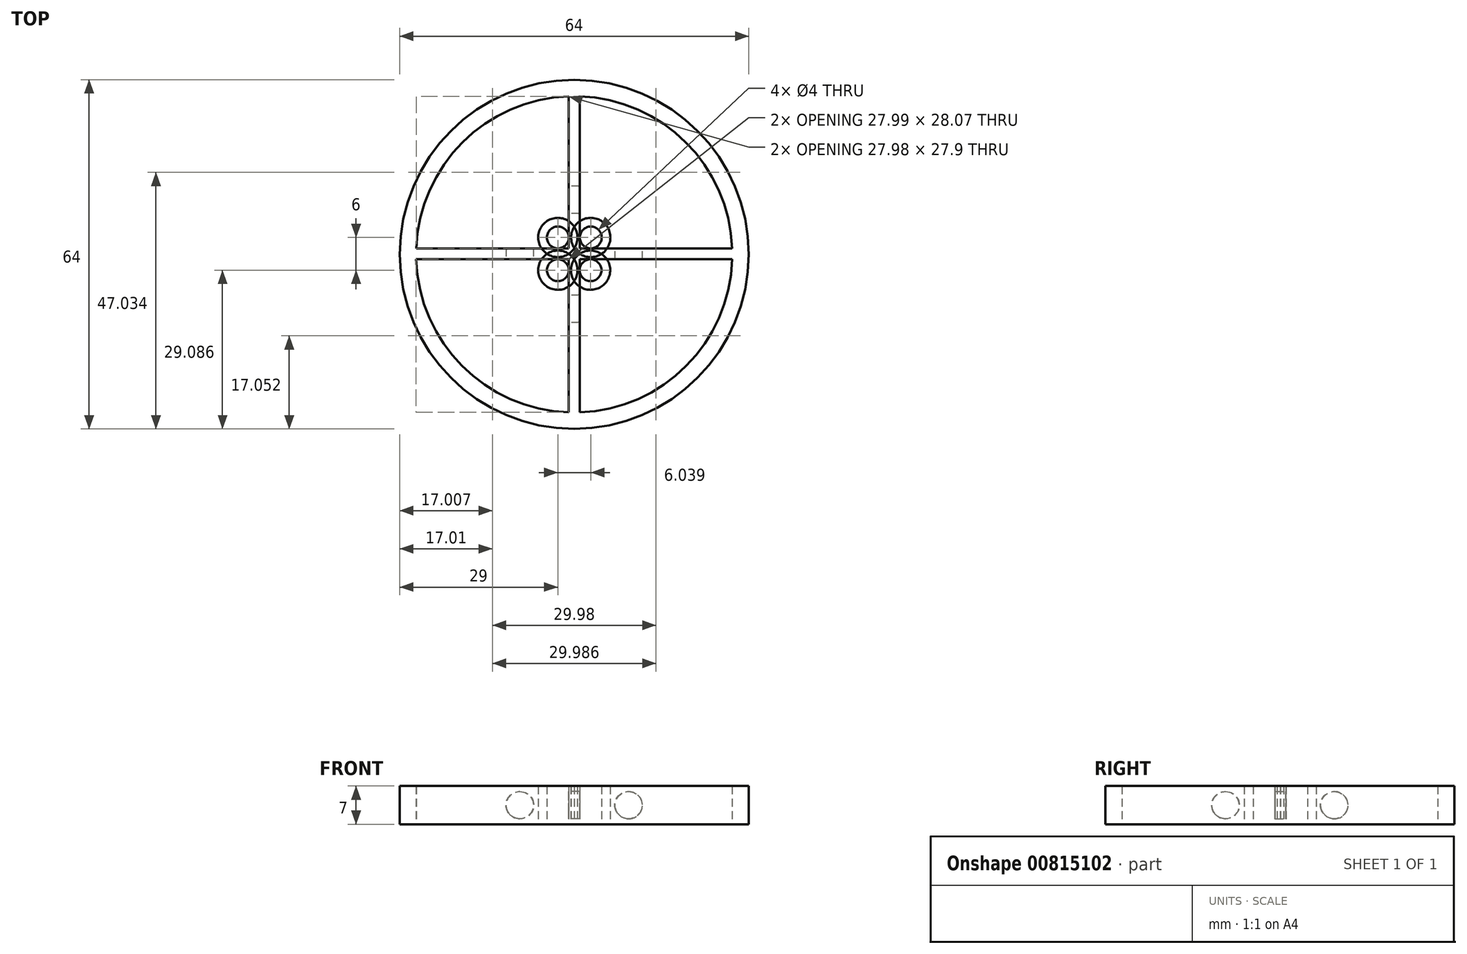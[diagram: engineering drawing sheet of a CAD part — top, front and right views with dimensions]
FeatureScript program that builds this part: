
annotation { "Feature Type Name" : "Feature", "Feature Type Description" : "" }
export const myFeature = defineFeature(function(context is Context, id is Id, definition is map)
    precondition{}
    {
        {
            var Q0;
            Q0=qCreatedBy(makeId("Top.planeOp"),FACE);
            var sketch = newSketch(context, id + "F0", { "sketchPlane" : qUnion([Q0])});
            skCircle(sketch, "E0", {"center": v(0, 0) * mm, "radius": 32 * mm});
            skCircle(sketch, "E1", {"center": v(0, 0) * mm, "radius": 29 * mm});
            skLineSegment(sketch, "E2.bottom", {"start": v(-1, 29.98) * mm, "end": v(1, 29.98) * mm});
            skLineSegment(sketch, "E2.top", {"start": v(-1, -29.98) * mm, "end": v(1, -29.98) * mm});
            skLineSegment(sketch, "E2.left", {"start": v(-1, 29.98) * mm, "end": v(-1, -29.98) * mm});
            skLineSegment(sketch, "E2.right", {"start": v(1, 29.98) * mm, "end": v(1, -29.98) * mm});
            skLineSegment(sketch, "E3.bottom", {"start": v(29.99, 1.09) * mm, "end": v(29.99, -0.91) * mm});
            skLineSegment(sketch, "E3.top", {"start": v(-29.98, 1.09) * mm, "end": v(-29.98, -0.91) * mm});
            skLineSegment(sketch, "E3.left", {"start": v(29.99, 1.09) * mm, "end": v(-29.98, 1.09) * mm});
            skLineSegment(sketch, "E3.right", {"start": v(29.99, -0.91) * mm, "end": v(-29.98, -0.91) * mm});
            skSolve(sketch);
        }
        {
            var Q0;
            Q0=makeQuery(id+"F0.imprint","IMPRINT",FACE,{"disambiguationData":[TD([[makeQuery(id+"F0.imprint","IMPRINT",EDGE,{"derivedFrom":sQuery(id+"F0.wireOp",EDGE,"E0")}),1.0]])]});
            var Q1;
            {var subQ0=sQuery(id+"F0.wireOp",EDGE,"E2.bottom");Q1=makeQuery(id+"F0.imprint","IMPRINT",FACE,{"disambiguationData":[TD([[makeQuery(id+"F0.imprint","IMPRINT",EDGE,{"derivedFrom":subQ0}),-1.0]])]});}
            var Q2;
            {var subQ5=sQuery(id+"F0.wireOp",EDGE,"E3.top");Q2=makeQuery(id+"F0.imprint","IMPRINT",FACE,{"disambiguationData":[TD([[makeQuery(id+"F0.imprint","IMPRINT",EDGE,{"derivedFrom":subQ5}),1.0]])]});}
            var Q3;
            {var subQ0=sQuery(id+"F0.wireOp",EDGE,"E2.top");Q3=makeQuery(id+"F0.imprint","IMPRINT",FACE,{"disambiguationData":[TD([[makeQuery(id+"F0.imprint","IMPRINT",EDGE,{"derivedFrom":subQ0}),1.0]])]});}
            var Q4;
            {var subQ0=sQuery(id+"F0.wireOp",EDGE,"E3.left");var subQ1=sQuery(id+"F0.wireOp",EDGE,"E2.left");var subQ2=makeQuery(id+"F0.imprint","INTERSECT",VERTEX,{"derivedFrom":[subQ1,subQ0]});Q4=makeQuery(id+"F0.imprint","IMPRINT",FACE,{"disambiguationData":[TD([[makeQuery(id+"F0.imprint","IMPRINT",EDGE,{"disambiguationData":[TD([[subQ2,-1.0]])],"derivedFrom":subQ1}),1.0]])]});}
            var Q5;
            {var subQ0=sQuery(id+"F0.wireOp",EDGE,"E3.left");var subQ1=sQuery(id+"F0.wireOp",EDGE,"E1");var subQ2=makeQuery(id+"F0.imprint","INTERSECT",VERTEX,{"disambiguationData":[OD(1.0)],"derivedFrom":[subQ1,subQ0]});Q5=makeQuery(id+"F0.imprint","IMPRINT",FACE,{"disambiguationData":[TD([[makeQuery(id+"F0.imprint","IMPRINT",EDGE,{"disambiguationData":[TD([[subQ2,-1.0]])],"derivedFrom":subQ1}),1.0]])]});}
            var Q6;
            {var subQ0=sQuery(id+"F0.wireOp",EDGE,"E3.left");var subQ1=sQuery(id+"F0.wireOp",EDGE,"E1");var subQ2=makeQuery(id+"F0.imprint","INTERSECT",VERTEX,{"disambiguationData":[OD(0.0)],"derivedFrom":[subQ1,subQ0]});Q6=makeQuery(id+"F0.imprint","IMPRINT",FACE,{"disambiguationData":[TD([[makeQuery(id+"F0.imprint","IMPRINT",EDGE,{"disambiguationData":[TD([[subQ2,1.0]])],"derivedFrom":subQ1}),1.0]])]});}
            var Q7;
            {var subQ0=sQuery(id+"F0.wireOp",EDGE,"E2.right");var subQ1=sQuery(id+"F0.wireOp",EDGE,"E1");var subQ2=makeQuery(id+"F0.imprint","INTERSECT",VERTEX,{"disambiguationData":[OD(0.0)],"derivedFrom":[subQ1,subQ0]});Q7=makeQuery(id+"F0.imprint","IMPRINT",FACE,{"disambiguationData":[TD([[makeQuery(id+"F0.imprint","IMPRINT",EDGE,{"disambiguationData":[TD([[subQ2,-1.0]])],"derivedFrom":subQ1}),1.0]])]});}
            var Q8;
            {var subQ0=sQuery(id+"F0.wireOp",EDGE,"E2.left");var subQ1=sQuery(id+"F0.wireOp",EDGE,"E1");var subQ2=makeQuery(id+"F0.imprint","INTERSECT",VERTEX,{"disambiguationData":[OD(1.0)],"derivedFrom":[subQ1,subQ0]});Q8=makeQuery(id+"F0.imprint","IMPRINT",FACE,{"disambiguationData":[TD([[makeQuery(id+"F0.imprint","IMPRINT",EDGE,{"disambiguationData":[TD([[subQ2,-1.0]])],"derivedFrom":subQ1}),1.0]])]});}
            var Q9;
            {var subQ5=sQuery(id+"F0.wireOp",EDGE,"E3.bottom");Q9=makeQuery(id+"F0.imprint","IMPRINT",FACE,{"disambiguationData":[TD([[makeQuery(id+"F0.imprint","IMPRINT",EDGE,{"derivedFrom":subQ5}),-1.0]])]});}
            extrude(context, id + "F1", {"entities" : qUnion([Q0, Q1, Q2, Q3, Q4, Q5, Q6, Q7, Q8, Q9]), "depth" : 7 * mm, "offsetDistance" : 25 * mm});
        }
        {
            var Q0;
            Q0=qCreatedBy(makeId("Right.planeOp"),FACE);
            var sketch = newSketch(context, id + "F2", { "sketchPlane" : qUnion([Q0])});
            skCircle(sketch, "E4", {"center": v(-10, 3.5) * mm, "radius": 2.5 * mm});
            skLineSegment(sketch, "E5", {"start": v(0, 0) * mm, "end": v(0, 19.73) * mm});
            skSolve(sketch);
        }
        {
            var Q0;
            Q0=makeQuery(id+"F2.imprint","IMPRINT",FACE,{"disambiguationData":[TD([[makeQuery(id+"F2.imprint","IMPRINT",EDGE,{"derivedFrom":sQuery(id+"F2.wireOp",EDGE,"E4")}),1.0]])]});
            var Q1;
            Q1=sQuery(id+"F2.wireOp",EDGE,"E5");
            revolve(context, id + "F3", {"operationType" : NewBodyOperationType.REMOVE, "surfaceOperationType" : NewSurfaceOperationType.NEW, "entities" : qUnion([Q0]), "axis" : qUnion([Q1]), "revolveType" : RevolveType.FULL});
        }
        {
            var Q0;
            Q0=qCreatedBy(makeId("Top.planeOp"),FACE);
            var sketch = newSketch(context, id + "F4", { "sketchPlane" : qUnion([Q0])});
            skCircle(sketch, "E6", {"center": v(3.04, 3.09) * mm, "radius": 2 * mm});
            skCircle(sketch, "E7", {"center": v(3.04, 3.09) * mm, "radius": 3.6 * mm});
            skCircle(sketch, "E8", {"center": v(3, -2.91) * mm, "radius": 2 * mm});
            skCircle(sketch, "E9", {"center": v(3, -2.91) * mm, "radius": 3.6 * mm});
            skCircle(sketch, "E10", {"center": v(-3, -2.91) * mm, "radius": 2 * mm});
            skCircle(sketch, "E11", {"center": v(-3, -2.91) * mm, "radius": 3.6 * mm});
            skCircle(sketch, "E12", {"center": v(-3, 3.09) * mm, "radius": 2 * mm});
            skCircle(sketch, "E13", {"center": v(-3, 3.09) * mm, "radius": 3.6 * mm});
            skSolve(sketch);
        }
        {
            var Q0;
            Q0=makeQuery(id+"F4.imprint","IMPRINT",FACE,{"disambiguationData":[TD([[makeQuery(id+"F4.imprint","IMPRINT",EDGE,{"derivedFrom":sQuery(id+"F4.wireOp",EDGE,"E6")}),-1.0]])]});
            var Q1;
            Q1=makeQuery(id+"F4.imprint","IMPRINT",FACE,{"disambiguationData":[TD([[makeQuery(id+"F4.imprint","IMPRINT",EDGE,{"derivedFrom":sQuery(id+"F4.wireOp",EDGE,"E8")}),-1.0]])]});
            var Q2;
            Q2=makeQuery(id+"F4.imprint","IMPRINT",FACE,{"disambiguationData":[TD([[makeQuery(id+"F4.imprint","IMPRINT",EDGE,{"derivedFrom":sQuery(id+"F4.wireOp",EDGE,"E10")}),-1.0]])]});
            var Q3;
            Q3=makeQuery(id+"F4.imprint","IMPRINT",FACE,{"disambiguationData":[TD([[makeQuery(id+"F4.imprint","IMPRINT",EDGE,{"derivedFrom":sQuery(id+"F4.wireOp",EDGE,"E12")}),-1.0]])]});
            extrude(context, id + "F5", {"entities" : qUnion([Q0, Q1, Q2, Q3]), "depth" : 7 * mm, "offsetDistance" : 25 * mm});
        }
    });
